# Revit family: VIESSMANN - Vitocal 350-G Pro 352 - C100
name_source: partatom
category: Mechanical Equipment
units: mm (PartAtom-declared; Revit-internal decimal feet)

## family parameters
Always vertical = Yes
Cut with Voids When Loaded = No
OmniClass Number = 23.75.10.21.17
OmniClass Title = Water-Source Heat Pumps
Part Type = Normal
Room Calculation Point = No
Round Connector Dimension = Use Diameter
Shared = No
Work Plane-Based = No

## types (2) — shared parameters
Autor = www.archispace.pl
Description = Vitocal 350-G PRO to kompaktowa, monowalentna pompa ciepła typu solanka/woda do ogrzewania, chłodzenia oraz podgrzewu wody użytkowej. Jako źródło ciepła można wykorzystać grunt, wodę gruntową lub powietrze zewnętrzne. Dzięki czterem typom, Vitocal 350-G PRO jest elastycznym rozwiązaniem grzewczym i chłodniczym, spełniającym indywidualne wymagania budynków mieszkalnych, komercyjnych i przemysłowych.
Długość całkowita = 2190 mm
Długość strefy serwisowej od przodu "e" = 700 mm  [stored 2.29659 ft]
Długość strefy serwisowej od tyłu "b" = 800 mm  [stored 2.62467 ft]
Długość strefy serwisowej od ściany lewej = 850 mm  [stored 2.78871 ft]
Długość strefy serwisowej od ściany prawej = 700 mm  [stored 2.29659 ft]
Manufacturer = Viessmann Sp. z o.o.
Masa urządzenia podstwowego = 1250.00 kg
Minimalna kubatura pomieszczenia = 36 m³
Model = Pompy ciepła solanka /woda Vitocal 350-G PRO o temperaturze zasilania do 75°C
Obieg pierwotny. Granica zabezpieczenia przed zamrożeniem. Źródła ciepła -  powietrze i zasobnik lodu = -25 °C
Obieg pierwotny. Granica zabezpieczenia przed zamrożeniem. Źródła ciepła - grunt i woda = -16 °C
Obieg pierwotny. Min. temperatura solanki na wlocie na granicy zabezpieczenia przed zamrożeniem –16,1°C (30% obj.) = -7 °C
Obieg pierwotny. Min. temperatura solanki na wlocie na granicy zabezpieczenia przed zamrożeniem –25,2°C (40% obj.) = -16 °C
Obieg pierwotny. Minimalny przepływ objętościowy (50% znamionowego przepływu objętościowego w przypadku B0/W35) = 11.8 m³/h
Obieg pierwotny. Pojemność wymiennika ciepła (solanka) = 13.1 L
Obieg pierwotny. Różnica temperatur = 3 K
Obieg wtórny. Maks. temperatura na zasilaniu obiegu wtórnego przy zasilaniu solanką z obiegu pierwotnego  B –7°C = 62 °C
Obieg wtórny. Maks. temperatura na zasilaniu obiegu wtórnego przy zasilaniu solanką z obiegu pierwotnego B od –1 do 25°CB –1 = 75 °C
Obieg wtórny. Maks. temperatura na zasilaniu obiegu wtórnego przy zasilaniu solanką z obiegu pierwotnego B –16°C = 56 °C
Obieg wtórny. Min. temperatura na zasilaniu zasobnika lodu = 29 °C
Obieg wtórny. Pojemność wymiennika ciepła (woda) = 17.2 L
Odstęp minimalny pompy ciepła od ściany = Odstęp minimalny pompy ciepła od ściany
Szerokość całkowita = 911 mm  [stored 2.98885 ft]
URL = https://www.viessmann.pl
Viessmann Kolor 1 = Viessmann Kolor 1
Waga przetwornicy częstotliwości wraz ze stelażem = 84.00 kg
Wysokość całkowita = 1652 mm
Zakres mocy = 17 - 100%
zero-valued in all types: Default Elevation

## per-type parameters (varying)
| type | Obieg pierwotny. Strata ciśnienia przy minimalnym przepływie | Obieg pierwotny. Strata ciśnienia przy znamionowym przepływie objętościowym | Obieg pierwotny. Znamionowy przepływ objętościowy | Obieg wtórny. Minimalny przepływ objętościowy | Obieg wtórny. Różnica temperatur | Obieg wtórny. Strata ciśnienia przy minimalnym przepływie objętościowym | Obieg wtórny. Strata ciśnienia przy znamionowym przepływie objętościowym | Obieg wtórny. Znamionowy przepływ objętościowy | Pobór mocy elektrycznej (bez pomp zewnętrznych) | Stopień efektywności ∊ (COP) | Wydajność chłodnicza | Znamionowa moc grzewcza | Znamionowe natężenie sprężarek (łącznie) |
| B0/W35 | 8.0 kPa | 26.0 kPa | 23.6 m³/h | 6.0 m³/h | 5 K | 1.0 kPa | 7.0 kPa | 17.6 m³/h | 27.6 kW | 3.69 | 75.4 kW | 101.9 kW | 41 A |
| B0/W55 | 4.0 kPa | 15.0 kPa | 17.3 m³/h | 3.0 m³/h | 8 K | 0.3 kPa | 2.0 kPa | 9.3 m³/h | 31.0 kW | 2.74 | 55.4 kW | 85.0 kW | 48 A |

note: [stored X ft] marks values corroborated as IEEE doubles in the binary element streams (Revit-internal decimal feet)

## geometry (parser evidence)
native form markers: Sweep x4
no freeform markers — native parametric forms only
